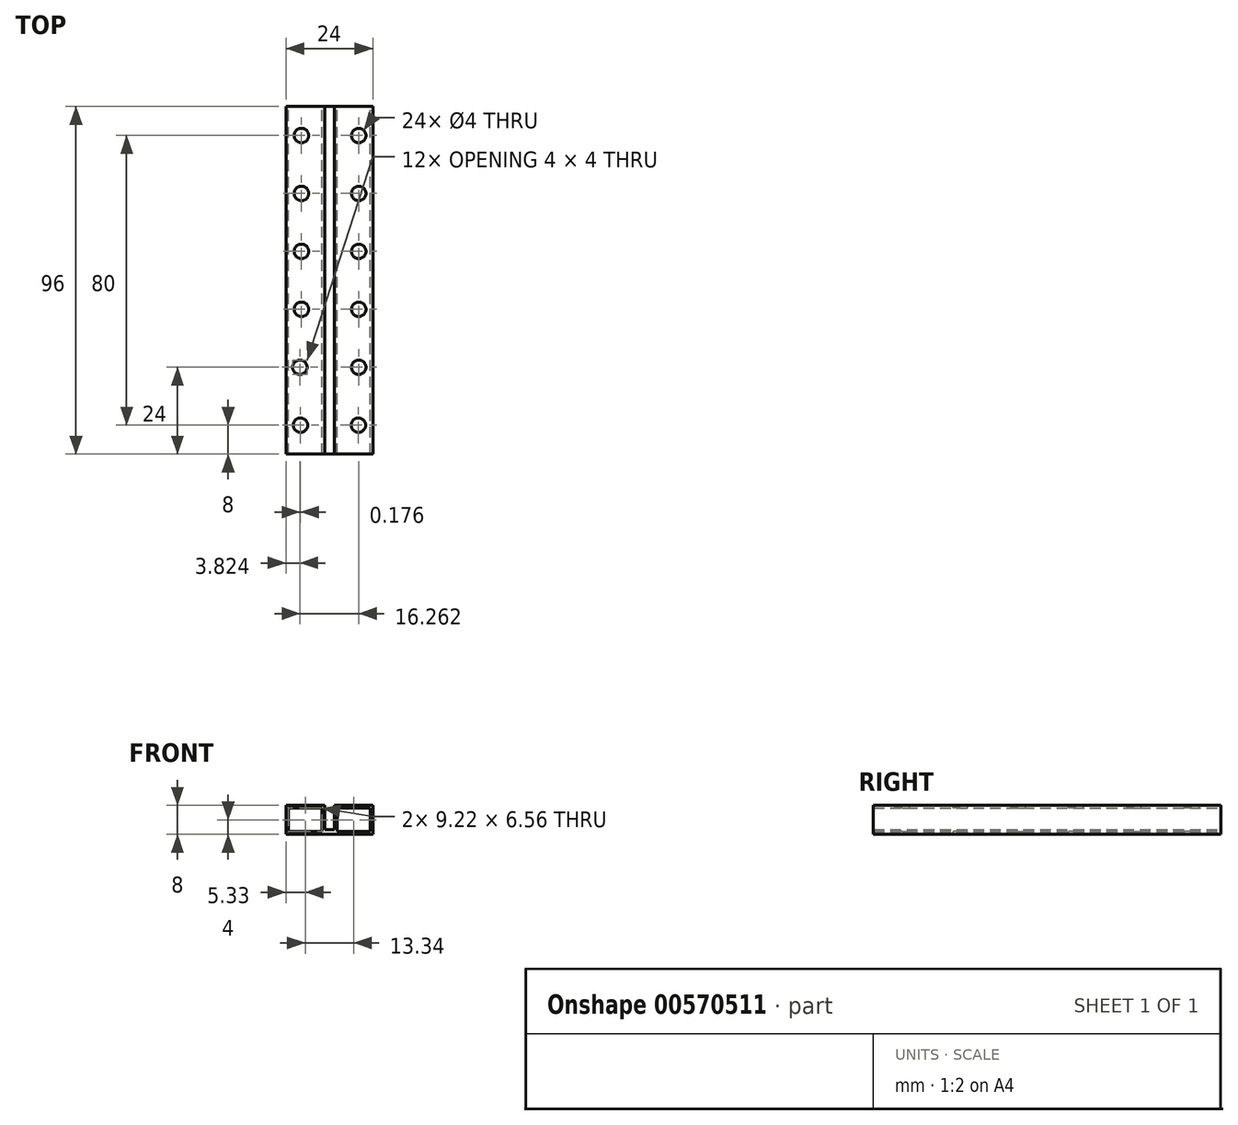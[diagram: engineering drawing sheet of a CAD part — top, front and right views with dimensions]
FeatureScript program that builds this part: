
annotation { "Feature Type Name" : "Feature", "Feature Type Description" : "" }
export const myFeature = defineFeature(function(context is Context, id is Id, definition is map)
    precondition{}
    {
        {
            var Q0;
            Q0=qCreatedBy(makeId("Front.planeOp"),FACE);
            var sketch = newSketch(context, id + "F0", { "sketchPlane" : qUnion([Q0])});
            skLineSegment(sketch, "E0.bottom", {"start": v(-12, 4) * mm, "end": v(12, 4) * mm});
            skLineSegment(sketch, "E0.top", {"start": v(-12, -4) * mm, "end": v(12, -4) * mm});
            skLineSegment(sketch, "E0.left", {"start": v(-12, 4) * mm, "end": v(-12, -4) * mm});
            skLineSegment(sketch, "E0.right", {"start": v(12, 4) * mm, "end": v(12, -4) * mm});
            skPoint(sketch, "E0.middle", {"position": v(0, 0) * mm});
            skLineSegment(sketch, "E1.bottom", {"start": v(-1.34, 10.75) * mm, "end": v(1.34, 10.75) * mm});
            skLineSegment(sketch, "E1.top", {"start": v(-1.34, -2.75) * mm, "end": v(1.34, -2.75) * mm});
            skLineSegment(sketch, "E1.left", {"start": v(-1.34, 10.75) * mm, "end": v(-1.34, -2.75) * mm});
            skLineSegment(sketch, "E1.right", {"start": v(1.34, 10.75) * mm, "end": v(1.34, -2.75) * mm});
            skPoint(sketch, "E1.middle", {"position": v(0, 4) * mm});
            skLineSegment(sketch, "E2.bottom", {"start": v(11.28, -3.28) * mm, "end": v(2.06, -3.28) * mm});
            skLineSegment(sketch, "E2.top", {"start": v(11.28, 3.28) * mm, "end": v(2.06, 3.28) * mm});
            skLineSegment(sketch, "E2.left", {"start": v(11.28, -3.28) * mm, "end": v(11.28, 3.28) * mm});
            skLineSegment(sketch, "E2.right", {"start": v(2.06, -3.28) * mm, "end": v(2.06, 3.28) * mm});
            skLineSegment(sketch, "E3.bottom", {"start": v(-2.06, 3.28) * mm, "end": v(-11.28, 3.28) * mm});
            skLineSegment(sketch, "E3.top", {"start": v(-2.06, -3.28) * mm, "end": v(-11.28, -3.28) * mm});
            skLineSegment(sketch, "E3.left", {"start": v(-2.06, 3.28) * mm, "end": v(-2.06, -3.28) * mm});
            skLineSegment(sketch, "E3.right", {"start": v(-11.28, 3.28) * mm, "end": v(-11.28, -3.28) * mm});
            skLineSegment(sketch, "E4.bottom", {"start": v(-9.78, 3.28) * mm, "end": v(-6.31, 3.28) * mm});
            skLineSegment(sketch, "E4.top", {"start": v(-9.78, -3.28) * mm, "end": v(-6.31, -3.28) * mm});
            skLineSegment(sketch, "E4.left", {"start": v(-9.78, 3.28) * mm, "end": v(-9.78, -3.28) * mm});
            skLineSegment(sketch, "E4.right", {"start": v(-6.31, 3.28) * mm, "end": v(-6.31, -3.28) * mm});
            skLineSegment(sketch, "E5.bottom", {"start": v(6.31, 3.28) * mm, "end": v(9.78, 3.28) * mm});
            skLineSegment(sketch, "E5.top", {"start": v(6.31, -3.28) * mm, "end": v(9.78, -3.28) * mm});
            skLineSegment(sketch, "E5.left", {"start": v(6.31, 3.28) * mm, "end": v(6.31, -3.28) * mm});
            skLineSegment(sketch, "E5.right", {"start": v(9.78, 3.28) * mm, "end": v(9.78, -3.28) * mm});
            skCircle(sketch, "E6", {"center": v(-8, 0) * mm, "radius": 2.16 * mm});
            skCircle(sketch, "E7", {"center": v(8, 0) * mm, "radius": 2.16 * mm});
            skSolve(sketch);
        }
        {
            var Q0;
            Q0=makeQuery(id+"F0.imprint","IMPRINT",FACE,{"disambiguationData":[TD([[makeQuery(id+"F0.imprint","IMPRINT",EDGE,{"derivedFrom":sQuery(id+"F0.wireOp",EDGE,"E0.top")}),1.0]])]});
            var Q1;
            {var subQ0=sQuery(id+"F0.wireOp",EDGE,"E4.bottom");Q1=makeQuery(id+"F0.imprint","IMPRINT",FACE,{"disambiguationData":[TD([[makeQuery(id+"F0.imprint","IMPRINT",EDGE,{"derivedFrom":subQ0}),-1.0]])]});}
            var Q2;
            {var subQ0=sQuery(id+"F0.wireOp",EDGE,"E4.top");Q2=makeQuery(id+"F0.imprint","IMPRINT",FACE,{"disambiguationData":[TD([[makeQuery(id+"F0.imprint","IMPRINT",EDGE,{"derivedFrom":subQ0}),1.0]])]});}
            var Q3;
            {var subQ0=sQuery(id+"F0.wireOp",EDGE,"E5.bottom");Q3=makeQuery(id+"F0.imprint","IMPRINT",FACE,{"disambiguationData":[TD([[makeQuery(id+"F0.imprint","IMPRINT",EDGE,{"derivedFrom":subQ0}),-1.0]])]});}
            var Q4;
            {var subQ0=sQuery(id+"F0.wireOp",EDGE,"E5.top");Q4=makeQuery(id+"F0.imprint","IMPRINT",FACE,{"disambiguationData":[TD([[makeQuery(id+"F0.imprint","IMPRINT",EDGE,{"derivedFrom":subQ0}),1.0]])]});}
            extrude(context, id + "F1", {"entities" : qUnion([Q0, Q1, Q2, Q3, Q4]), "depth" : 96 * mm, "offsetDistance" : 25 * mm});
        }
        {
            var Q0;
            {var subQ0=sQuery(id+"F0.wireOp",EDGE,"E0.bottom");Q0=makeQuery(id+"F1.opExtrude","SWEPT_FACE",FACE,{"disambiguationData":[OSD([subQ0]),TDD([makeQuery(id+"F0.imprint","IMPRINT",EDGE,{"disambiguationData":[TD([[makeQuery(id+"F0.imprint","INTERSECT",VERTEX,{"derivedFrom":[subQ0,sQuery(id+"F0.wireOp",EDGE,"E0.right")]}),1.0]])],"derivedFrom":subQ0})])]});}
            var sketch = newSketch(context, id + "F2", { "sketchPlane" : qUnion([Q0])});
            skCircle(sketch, "E8", {"center": v(8, -88) * mm, "radius": 2 * mm});
            skCircle(sketch, "E9", {"center": v(-8, -88) * mm, "radius": 2 * mm});
            skCircle(sketch, "E10", {"center": v(8.09, -72) * mm, "radius": 2 * mm});
            skCircle(sketch, "E11", {"center": v(-8.18, -72) * mm, "radius": 2 * mm});
            skCircle(sketch, "E12", {"center": v(8.09, -56) * mm, "radius": 2 * mm});
            skCircle(sketch, "E13", {"center": v(-7.73, -56) * mm, "radius": 2 * mm});
            skCircle(sketch, "E14", {"center": v(8.09, -40) * mm, "radius": 2 * mm});
            skCircle(sketch, "E15", {"center": v(-7.73, -40) * mm, "radius": 2 * mm});
            skCircle(sketch, "E16", {"center": v(8.09, -24) * mm, "radius": 2 * mm});
            skCircle(sketch, "E17", {"center": v(-7.73, -24) * mm, "radius": 2 * mm});
            skCircle(sketch, "E18", {"center": v(8.09, -8) * mm, "radius": 2 * mm});
            skCircle(sketch, "E19", {"center": v(-7.73, -8) * mm, "radius": 2 * mm});
            skSolve(sketch);
        }
        {
            var Q0;
            Q0=makeQuery(id+"F2.imprint","IMPRINT",FACE,{"disambiguationData":[TD([[makeQuery(id+"F2.imprint","IMPRINT",EDGE,{"derivedFrom":sQuery(id+"F2.wireOp",EDGE,"E9")}),1.0]])]});
            var Q1;
            Q1=makeQuery(id+"F2.imprint","IMPRINT",FACE,{"disambiguationData":[TD([[makeQuery(id+"F2.imprint","IMPRINT",EDGE,{"derivedFrom":sQuery(id+"F2.wireOp",EDGE,"E8")}),1.0]])]});
            var Q2;
            Q2=makeQuery(id+"F2.imprint","IMPRINT",FACE,{"disambiguationData":[TD([[makeQuery(id+"F2.imprint","IMPRINT",EDGE,{"derivedFrom":sQuery(id+"F2.wireOp",EDGE,"E11")}),1.0]])]});
            var Q3;
            Q3=makeQuery(id+"F2.imprint","IMPRINT",FACE,{"disambiguationData":[TD([[makeQuery(id+"F2.imprint","IMPRINT",EDGE,{"derivedFrom":sQuery(id+"F2.wireOp",EDGE,"E10")}),1.0]])]});
            var Q4;
            Q4=makeQuery(id+"F2.imprint","IMPRINT",FACE,{"disambiguationData":[TD([[makeQuery(id+"F2.imprint","IMPRINT",EDGE,{"derivedFrom":sQuery(id+"F2.wireOp",EDGE,"E13")}),1.0]])]});
            var Q5;
            Q5=makeQuery(id+"F2.imprint","IMPRINT",FACE,{"disambiguationData":[TD([[makeQuery(id+"F2.imprint","IMPRINT",EDGE,{"derivedFrom":sQuery(id+"F2.wireOp",EDGE,"E12")}),1.0]])]});
            var Q6;
            Q6=makeQuery(id+"F2.imprint","IMPRINT",FACE,{"disambiguationData":[TD([[makeQuery(id+"F2.imprint","IMPRINT",EDGE,{"derivedFrom":sQuery(id+"F2.wireOp",EDGE,"E15")}),1.0]])]});
            var Q7;
            Q7=makeQuery(id+"F2.imprint","IMPRINT",FACE,{"disambiguationData":[TD([[makeQuery(id+"F2.imprint","IMPRINT",EDGE,{"derivedFrom":sQuery(id+"F2.wireOp",EDGE,"E14")}),1.0]])]});
            var Q8;
            Q8=makeQuery(id+"F2.imprint","IMPRINT",FACE,{"disambiguationData":[TD([[makeQuery(id+"F2.imprint","IMPRINT",EDGE,{"derivedFrom":sQuery(id+"F2.wireOp",EDGE,"E17")}),1.0]])]});
            var Q9;
            Q9=makeQuery(id+"F2.imprint","IMPRINT",FACE,{"disambiguationData":[TD([[makeQuery(id+"F2.imprint","IMPRINT",EDGE,{"derivedFrom":sQuery(id+"F2.wireOp",EDGE,"E16")}),1.0]])]});
            var Q10;
            Q10=makeQuery(id+"F2.imprint","IMPRINT",FACE,{"disambiguationData":[TD([[makeQuery(id+"F2.imprint","IMPRINT",EDGE,{"derivedFrom":sQuery(id+"F2.wireOp",EDGE,"E18")}),1.0]])]});
            var Q11;
            Q11=makeQuery(id+"F2.imprint","IMPRINT",FACE,{"disambiguationData":[TD([[makeQuery(id+"F2.imprint","IMPRINT",EDGE,{"derivedFrom":sQuery(id+"F2.wireOp",EDGE,"E19")}),1.0]])]});
            extrude(context, id + "F3", {"entities" : qUnion([Q0, Q1, Q2, Q3, Q4, Q5, Q6, Q7, Q8, Q9, Q10, Q11]), "operationType" : NewBodyOperationType.REMOVE, "oppositeDirection" : true, "depth" : 8.1 * mm, "offsetDistance" : 25 * mm});
        }
    });
